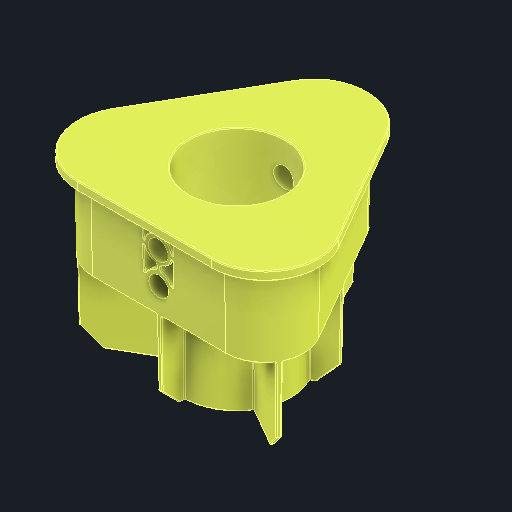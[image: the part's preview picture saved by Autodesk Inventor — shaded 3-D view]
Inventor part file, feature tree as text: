
AUTODESK INVENTOR PART (.ipt)
format: ipt  version: 2024.2 (Build 282272000, 272)  size: 1,730,560 bytes
history: native  units: in
note: dims shown in document units (in); Inventor stores cm internally (conversion verified against a paired STEP export)
features: fillet x1
ambient origin geometry x8: Origin, YZ Plane, XZ Plane, XY Plane, X Axis, Y Axis, Z Axis, Center Point
bodies: Solid1 (feature_tree)
feature tree (1):
  fillet  "Fillet45"  [1 undecoded]
note: 1 required parameter value undecoded (feature->parameter linkage not recoverable at this tier; creation-order binding heuristic only, values carry confidence <= 0.55)
